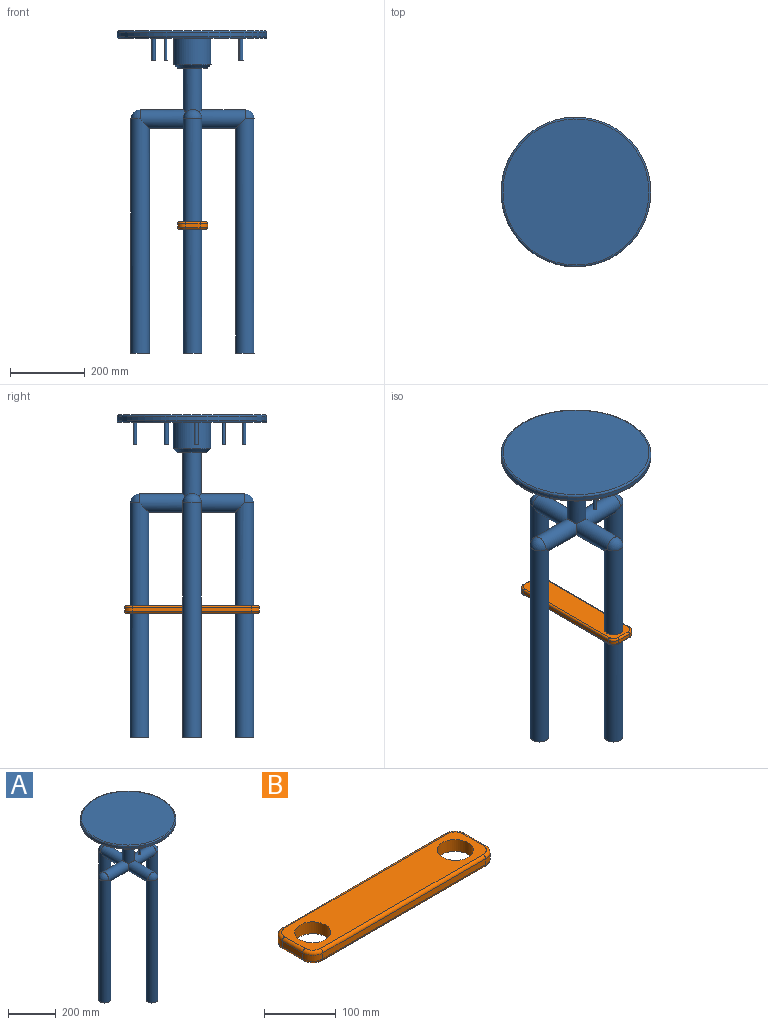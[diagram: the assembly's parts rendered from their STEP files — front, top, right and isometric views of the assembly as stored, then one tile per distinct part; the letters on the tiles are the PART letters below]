
ASSEMBLY  parts=2 mates=1
PART A: 35 faces, bbox 433x433x860 mm
  f0: plane 80x80mm, normal (0,0,-1), area 3063.1mm2, adj f5,f10
  f1: cylinder r=200mm len=400mm, axis (0,0,1), area 12566.4mm2, adj f23,f24
  f2: plane 390x390mm, normal (0,0,1), area 119459.1mm2, adj f24
  f3: plane 390x390mm, normal (0,0,-1), area 111267.1mm2, adj f4,f23,f25,f27,f29,f31,f33
  f4: cylinder r=50mm len=100mm, axis (0,0,1), area 21991.1mm2, adj f3,f5
  f5: cone r=40mm half-angle=45deg, axis (0,0,1), area 3998.6mm2, adj f0,f4
  f6: plane 50x50mm, normal (0,0,-1), area 1963.5mm2, adj f19
  f7: plane 50x50mm, normal (0,0,-1), area 1963.5mm2, adj f21
  f8: plane 50x50mm, normal (0,0,-1), area 1963.5mm2, adj f17
  f9: plane 50x50mm, normal (0,0,-1), area 1963.5mm2, adj f15
  f10: cylinder r=25mm len=117.32mm, axis (0,0,-1), area 17670.2mm2, adj f0,f11,f12,f13,f14
  f11: cylinder r=25mm len=140mm, axis (-1,0,0), area 17723.4mm2, adj f10,f12,f13,f19,f20
  f12: cylinder r=25mm len=140mm, axis (0,1,0), area 17723.4mm2, adj f10,f11,f14,f21,f22
  f13: cylinder r=25mm len=140mm, axis (0,-1,0), area 17723.4mm2, adj f10,f11,f14,f15,f16
  f14: cylinder r=25mm len=140mm, axis (-1,0,0), area 17723.4mm2, adj f10,f12,f13,f17,f18
  f15: cylinder r=25mm len=625mm, axis (0,0,1), area 96924.8mm2, adj f9,f13,f16
  f16: sphere r=25mm, area 1963.5mm2, adj f13,f15
  f17: cylinder r=25mm len=625mm, axis (0,0,-1), area 96924.8mm2, adj f8,f14,f18
  f18: sphere r=25mm, area 1963.5mm2, adj f14,f17
  f19: cylinder r=25mm len=625mm, axis (0,0,-1), area 96924.8mm2, adj f6,f11,f20
  f20: sphere r=25mm, area 1963.5mm2, adj f11,f19
  f21: cylinder r=25mm len=625mm, axis (0,0,-1), area 96924.8mm2, adj f7,f12,f22
  f22: sphere r=25mm, area 1963.5mm2, adj f12,f21
  f23: torus R=195mm, axis (0,0,1), area 9779.9mm2, adj f1,f3
  f24: torus R=195mm, axis (0,0,1), area 9779.9mm2, adj f1,f2
  f25: cylinder r=4mm len=60mm, axis (0,0,-1), area 1508mm2, adj f3,f26
  f26: plane 8x8mm, normal (0,0,-1), area 50.3mm2, adj f25
  f27: cylinder r=4.86mm len=60mm, axis (0,0,-1), area 1830.8mm2, adj f3,f28
  f28: plane 9.71x9.71mm, normal (0,0,-1), area 74.1mm2, adj f27
  f29: cylinder r=4mm len=60mm, axis (0,0,-1), area 1508mm2, adj f3,f30
  f30: plane 8x8mm, normal (0,0,-1), area 50.3mm2, adj f29
  f31: cylinder r=6mm len=60mm, axis (0,0,-1), area 2261.9mm2, adj f3,f32
  f32: plane 12x12mm, normal (0,0,-1), area 113.1mm2, adj f31
  f33: cylinder r=4mm len=60mm, axis (0,0,-1), area 1508mm2, adj f3,f34
  f34: plane 8x8mm, normal (0,0,-1), area 50.3mm2, adj f33
PART B: 28 faces, bbox 363.3x83.3x20 mm
  f0: plane 320x10mm, normal (0,-1,0), area 3200mm2, adj f9,f10,f12,f27
  f1: plane 320x10mm, normal (0,1,0), area 3200mm2, adj f8,f11,f19,f20
  f2: plane 350x70mm, normal (0,0,1), area 20379.9mm2, adj f6,f7,f20,f21,f22,f23,f24,f25
  f3: plane 350x70mm, normal (0,0,-1), area 20379.9mm2, adj f6,f7,f12,f13,f14,f15,f16,f17
  f4: plane 40x10mm, normal (1,0,0), area 400mm2, adj f8,f9,f15,f23
  f5: plane 40x10mm, normal (-1,0,0), area 400mm2, adj f10,f11,f16,f24
  f6: cylinder r=25mm len=50mm, axis (0,0,1), area 3141.6mm2, adj f2,f3
  f7: cylinder r=25mm len=50mm, axis (0,0,1), area 3141.6mm2, adj f2,f3
  f8: cylinder r=20mm len=20mm, axis (0,0,-1), area 314.2mm2, adj f1,f4,f17,f21
  f9: cylinder r=20mm len=20mm, axis (0,0,1), area 314.2mm2, adj f0,f4,f13,f25
  f10: cylinder r=20mm len=20mm, axis (0,0,-1), area 314.2mm2, adj f0,f5,f14,f26
  f11: cylinder r=20mm len=20mm, axis (0,0,1), area 314.2mm2, adj f1,f5,f18,f22
  f12: cylinder r=5mm len=320mm, axis (-1,0,0), area 2513.3mm2, adj f0,f3,f13,f14
  f13: torus R=15mm, axis (0,0,1), area 224.3mm2, adj f3,f9,f12,f15
  f14: torus R=15mm, axis (0,0,1), area 224.3mm2, adj f3,f10,f12,f16
  f15: cylinder r=5mm len=40mm, axis (0,-1,0), area 314.2mm2, adj f3,f4,f13,f17
  f16: cylinder r=5mm len=40mm, axis (0,1,0), area 314.2mm2, adj f3,f5,f14,f18
  f17: torus R=15mm, axis (0,0,1), area 224.3mm2, adj f3,f8,f15,f19
  f18: torus R=15mm, axis (0,0,1), area 224.3mm2, adj f3,f11,f16,f19
  f19: cylinder r=5mm len=320mm, axis (1,0,0), area 2513.3mm2, adj f1,f3,f17,f18
  f20: cylinder r=5mm len=320mm, axis (-1,0,0), area 2513.3mm2, adj f1,f2,f21,f22
  f21: torus R=15mm, axis (0,0,1), area 224.3mm2, adj f2,f8,f20,f23
  f22: torus R=15mm, axis (0,0,1), area 224.3mm2, adj f2,f11,f20,f24
  f23: cylinder r=5mm len=40mm, axis (0,1,0), area 314.2mm2, adj f2,f4,f21,f25
  f24: cylinder r=5mm len=40mm, axis (0,-1,0), area 314.2mm2, adj f2,f5,f22,f26
  f25: torus R=15mm, axis (0,0,1), area 224.3mm2, adj f2,f9,f23,f27
  f26: torus R=15mm, axis (0,0,1), area 224.3mm2, adj f2,f10,f24,f27
  f27: cylinder r=5mm len=320mm, axis (1,0,0), area 2513.3mm2, adj f0,f2,f25,f26
PLACE A t=(-223.18,80.72,11.25)mm fixed
PLACE B rot(axis=(0,0,-1),90deg) t=(-263.18,1726.28,-517.98)mm
MATE slider A.f21 <-> B.f6  axis (0,0,-1) through (-223.18,-59.28,-828.75)mm
